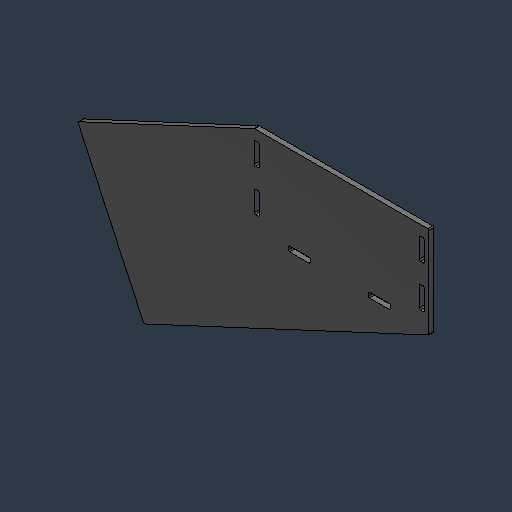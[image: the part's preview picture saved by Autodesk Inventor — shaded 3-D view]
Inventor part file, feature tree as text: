
AUTODESK INVENTOR PART (.ipt)
format: ipt  version: 2024.3 (Build 283343000, 343)  size: 119,808 bytes
history: native  units: mm (DEFAULTED — no unit token found)
features: fillet x1
ambient origin geometry x8: Origin, YZ Plane, XZ Plane, XY Plane, X Axis, Y Axis, Z Axis, Center Point
bodies: Solid1 (feature_tree)
feature tree (1):
  fillet  "Fillet1"  [1 undecoded]
note: 1 required parameter value undecoded (feature->parameter linkage not recoverable at this tier; creation-order binding heuristic only, values carry confidence <= 0.55)
